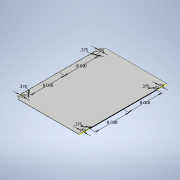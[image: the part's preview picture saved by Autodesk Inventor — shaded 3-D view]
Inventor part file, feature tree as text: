
AUTODESK INVENTOR PART (.ipt)
format: ipt  version: 2021 (Build 250183000, 183)  size: 150,528 bytes
history: native  units: in
note: dims shown in document units (in); Inventor stores cm internally (conversion verified against a paired STEP export)
features: extrude x2, sketch x2, hole x1
ambient origin geometry x8: Origin, YZ Plane, XZ Plane, XY Plane, X Axis, Y Axis, Z Axis, Center Point
bodies: Solid1 (feature_tree)
feature tree (5):
  extrude  "Extrusion1"  Depth=10.5in
  sketch  "Sketch2"  dims[d14=10.5in d15=10.5in d16=10.5in d17=0.06in d18=0.0in d19=6.5in d20=1.25in d21=5.1in d22=1.25in d23=1.25in d24=1.25in d25=6.5in d26=5.1in d27=1.25in d28=1.25in d29=8.0in d30=0.75in d31=0.375in d32=8.0in d33=0.75in d34=0.375in d35=8.0in d36=0.75in d37=8.0in d38=0.75in d39=0.375in d40=0.375in d41=1.0in d42=0.0in d43=0.201in d44=0.75in d45=0.385in d46=0.25in d47=0.5635in d48=1.0in d49=0.8108in]
  extrude  "Extrusion2"  Depth=10.5in
  hole  "Hole1"  [1 undecoded]
  sketch  "Sketch1"  dims[d12=15.28in d13=10.5in]
note: 1 required parameter value undecoded (feature->parameter linkage not recoverable at this tier; creation-order binding heuristic only, values carry confidence <= 0.55)
